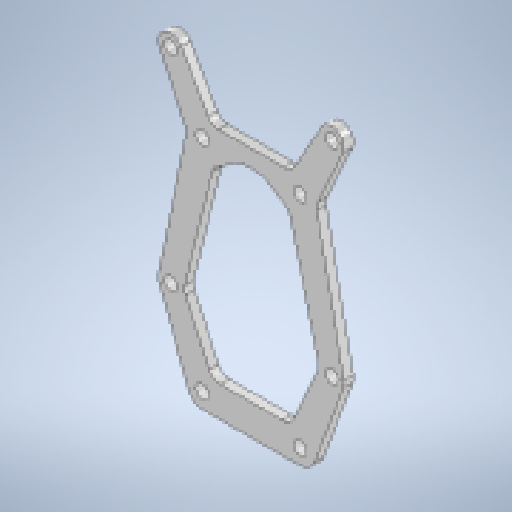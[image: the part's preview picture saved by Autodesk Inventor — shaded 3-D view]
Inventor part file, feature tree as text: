
AUTODESK INVENTOR PART (.ipt)
format: ipt  version: 2025.1 (Build 291241000, 241)  size: 231,936 bytes
history: native  units: mm
features: other x9, reference x9, extrude x1, fillet x1, sketch x1
ambient origin geometry x8: Origin, YZ Plane, XZ Plane, XY Plane, X Axis, Y Axis, Z Axis, Center Point
bodies: Body1 (feature_tree)
feature tree (21):
  other  "ソリッド1"
  extrude  "押し出し1"  Depth=2.2mm
  fillet  "フィレット1"  Radius=2.2mm
  sketch  "スケッチ1"
  reference  "参照1"
  reference  "参照2"
  reference  "参照3"
  reference  "参照4"
  reference  "参照5"
  reference  "参照6"
  reference  "参照7"
  reference  "参照8"
  reference  "参照9"
  other  "<userpath>\Documents\Inventor\Vixen\doutai.iam"
  other  "doutai.iam"
  other  "KRS2500_scale:1"
  other  "KSHI:1"
  other  "mata3:3"
  other  "mata3:4"
  other  "mata3:1"
  other  "mata3:2"
